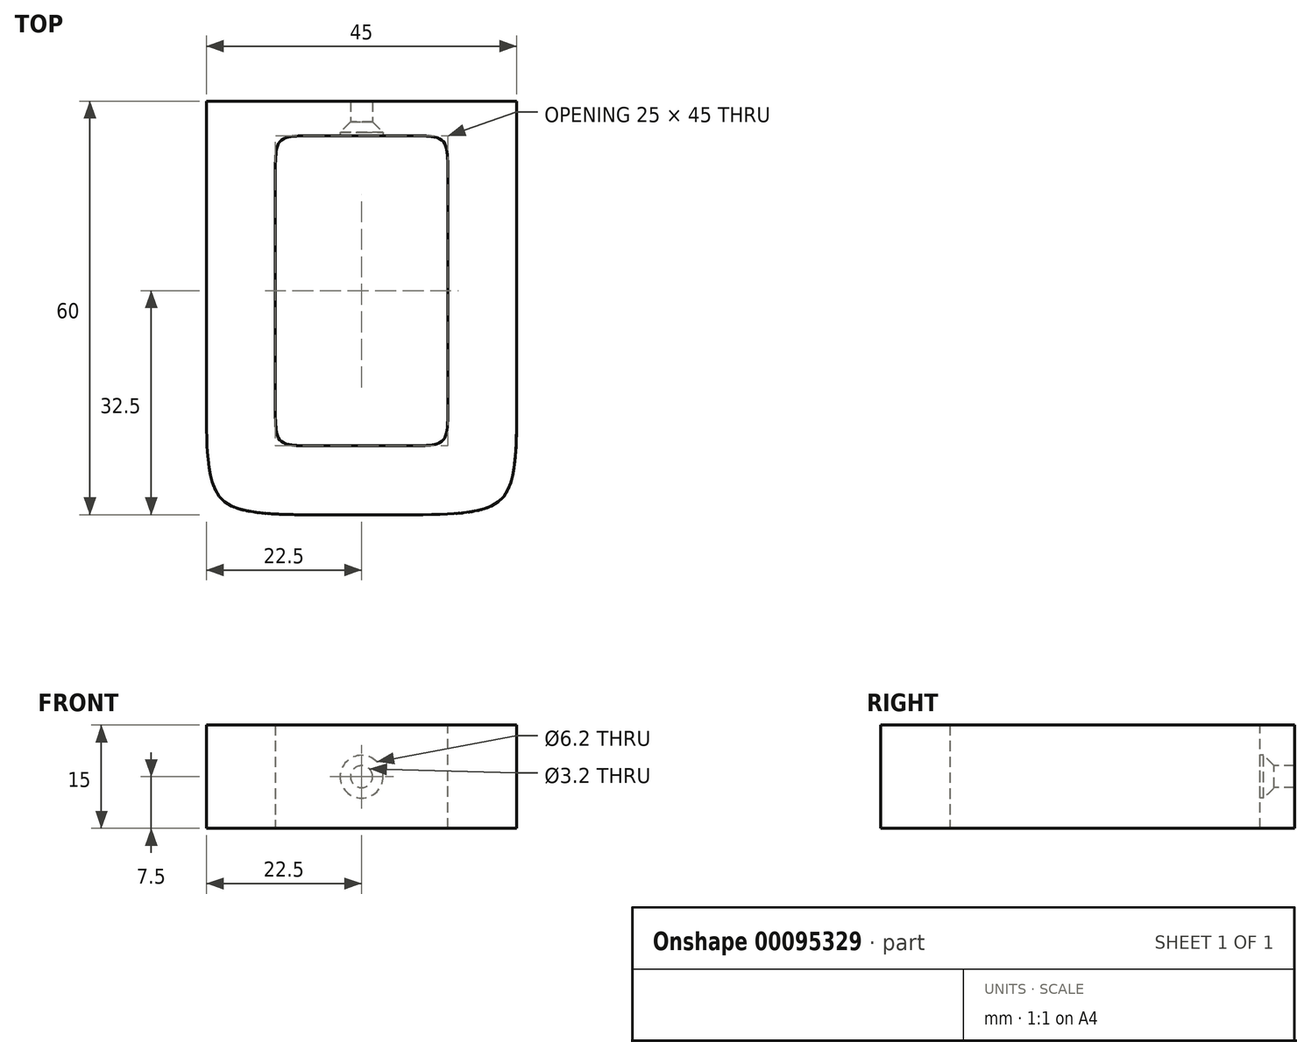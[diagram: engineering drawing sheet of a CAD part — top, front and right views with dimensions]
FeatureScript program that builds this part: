
annotation { "Feature Type Name" : "Feature", "Feature Type Description" : "" }
export const myFeature = defineFeature(function(context is Context, id is Id, definition is map)
    precondition{}
    {
        {
            var Q0;
            Q0=qCreatedBy(makeId("Top.planeOp"),FACE);
            var sketch = newSketch(context, id + "F0", { "sketchPlane" : qUnion([Q0])});
            skLineSegment(sketch, "E0.bottom", {"start": v(-22.5, 0) * mm, "end": v(22.5, 0) * mm});
            skLineSegment(sketch, "E0.top", {"start": v(-22.5, -60) * mm, "end": v(22.5, -60) * mm});
            skLineSegment(sketch, "E0.left", {"start": v(-22.5, 0) * mm, "end": v(-22.5, -60) * mm});
            skLineSegment(sketch, "E0.right", {"start": v(22.5, 0) * mm, "end": v(22.5, -60) * mm});
            skLineSegment(sketch, "E1.bottom", {"start": v(-12.5, -5) * mm, "end": v(12.5, -5) * mm});
            skLineSegment(sketch, "E1.top", {"start": v(-12.5, -50) * mm, "end": v(12.5, -50) * mm});
            skLineSegment(sketch, "E1.left", {"start": v(-12.5, -5) * mm, "end": v(-12.5, -50) * mm});
            skLineSegment(sketch, "E1.right", {"start": v(12.5, -5) * mm, "end": v(12.5, -50) * mm});
            skLineSegment(sketch, "E2", {"start": v(0, -50) * mm, "end": v(0, -60) * mm, "construction": true});
            skLineSegment(sketch, "E3", {"start": v(12.5, -50) * mm, "end": v(22.5, -50) * mm, "construction": true});
            skSolve(sketch);
        }
        {
            var Q0;
            Q0 = qSketchRegion(id + "F0", true);
            extrude(context, id + "F1", {"entities" : qUnion([Q0]), "endBound" : BoundingType.SYMMETRIC, "depth" : 15 * mm});
        }
        {
            var Q0;
            Q0=qCreatedBy(makeId("Top.planeOp"),FACE);
            var sketch = newSketch(context, id + "F2", { "sketchPlane" : qUnion([Q0])});
            skLineSegment(sketch, "E4", {"start": v(0, 0) * mm, "end": v(0, -5) * mm});
            skLineSegment(sketch, "E5", {"start": v(0, -5) * mm, "end": v(3.1, -5) * mm});
            skLineSegment(sketch, "E6", {"start": v(3.1, -5) * mm, "end": v(3.1, -4.5) * mm});
            skLineSegment(sketch, "E7", {"start": v(3.1, -4.5) * mm, "end": v(1.6, -3) * mm});
            skLineSegment(sketch, "E8", {"start": v(1.6, -3) * mm, "end": v(1.6, 0) * mm});
            skLineSegment(sketch, "E9", {"start": v(1.6, 0) * mm, "end": v(0, 0) * mm});
            skSolve(sketch);
        }
        {
            var Q0;
            Q0 = qSketchRegion(id + "F2", true);
            var Q1;
            Q1=sQuery(id+"F2.wireOp",EDGE,"E4");
            revolve(context, id + "F3", {"operationType" : NewBodyOperationType.REMOVE, "entities" : qUnion([Q0]), "axis" : qUnion([Q1]), "revolveType" : RevolveType.FULL, "oppositeDirection" : true});
        }
        {
            var Q0;
            Q0=makeQuery(id+"F1.opExtrude","SWEPT_EDGE",EDGE,{"disambiguationData":[OSD([sQuery(id+"F0.wireOp",EDGE,"E1.bottom"),sQuery(id+"F0.wireOp",EDGE,"E1.left")])]});
            var Q1;
            Q1=makeQuery(id+"F1.opExtrude","SWEPT_EDGE",EDGE,{"disambiguationData":[OSD([sQuery(id+"F0.wireOp",EDGE,"E1.bottom"),sQuery(id+"F0.wireOp",EDGE,"E1.right")])]});
            var Q2;
            Q2=makeQuery(id+"F1.opExtrude","SWEPT_EDGE",EDGE,{"disambiguationData":[OSD([sQuery(id+"F0.wireOp",EDGE,"E1.top"),sQuery(id+"F0.wireOp",EDGE,"E1.left")])]});
            var Q3;
            Q3=makeQuery(id+"F1.opExtrude","SWEPT_EDGE",EDGE,{"disambiguationData":[OSD([sQuery(id+"F0.wireOp",EDGE,"E1.top"),sQuery(id+"F0.wireOp",EDGE,"E1.right")])]});
            fillet(context, id + "F4", {"entities" : qUnion([Q0, Q1, Q2, Q3]), "radius" : 5 * mm, "tangentPropagation" : true, "rho" : .7, "crossSection" : FilletCrossSection.CONIC, "allowEdgeOverflow" : false});
        }
        {
            var Q0;
            Q0=makeQuery(id+"F1.opExtrude","SWEPT_EDGE",EDGE,{"disambiguationData":[OSD([sQuery(id+"F0.wireOp",EDGE,"E0.top"),sQuery(id+"F0.wireOp",EDGE,"E0.left")])]});
            var Q1;
            Q1=makeQuery(id+"F1.opExtrude","SWEPT_EDGE",EDGE,{"disambiguationData":[OSD([sQuery(id+"F0.wireOp",EDGE,"E0.top"),sQuery(id+"F0.wireOp",EDGE,"E0.right")])]});
            fillet(context, id + "F5", {"entities" : qUnion([Q0, Q1]), "radius" : 15 * mm, "tangentPropagation" : true, "rho" : .7, "crossSection" : FilletCrossSection.CONIC, "allowEdgeOverflow" : false});
        }
    });
